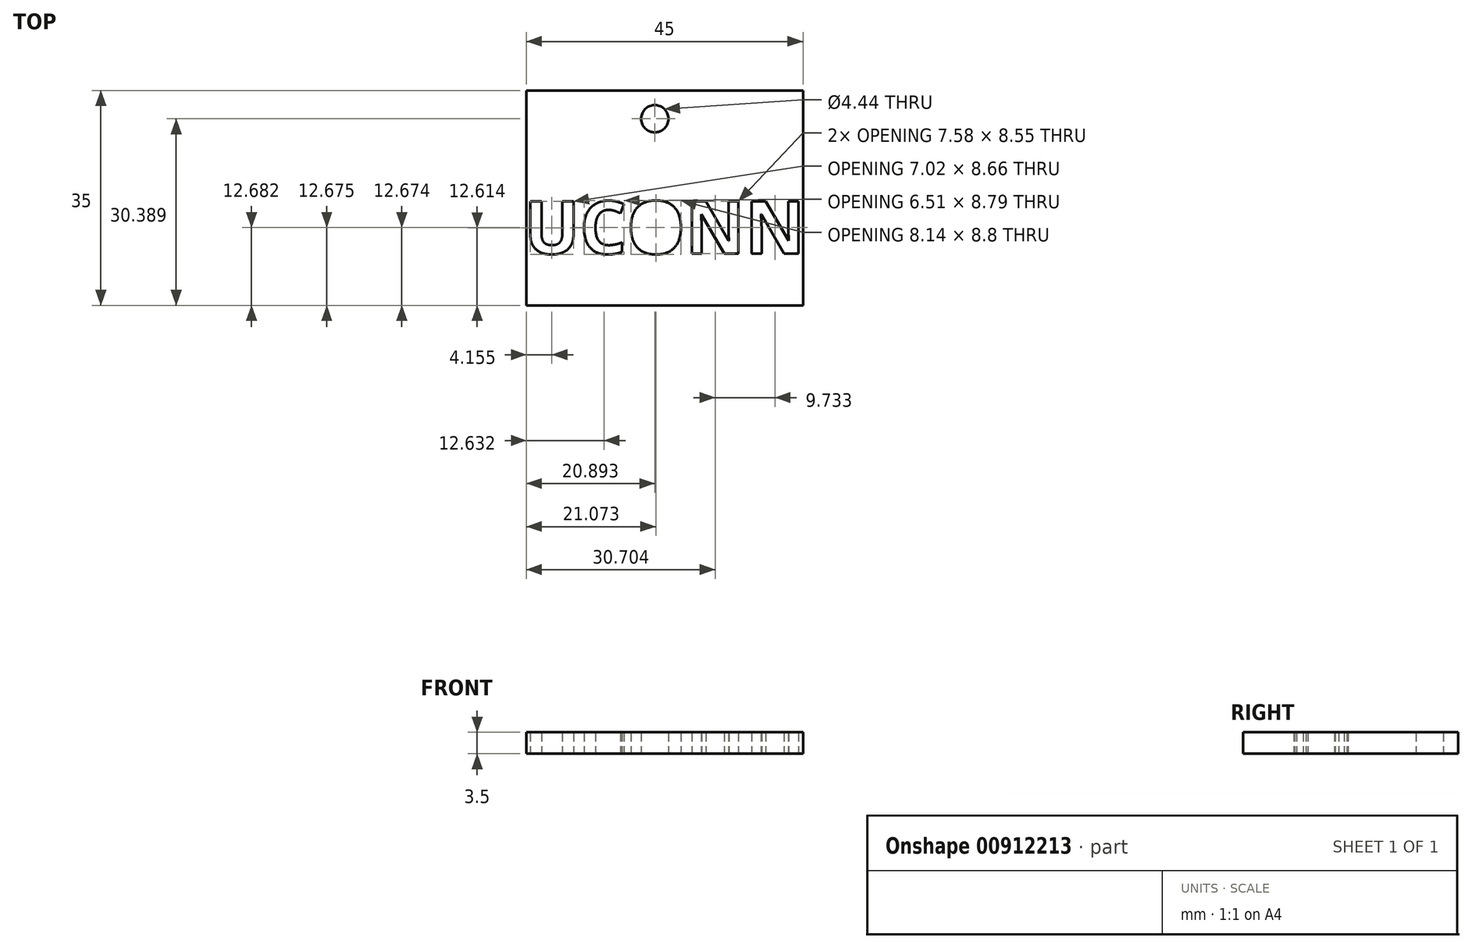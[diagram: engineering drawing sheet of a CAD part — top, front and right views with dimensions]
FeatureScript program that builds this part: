
annotation { "Feature Type Name" : "Feature", "Feature Type Description" : "" }
export const myFeature = defineFeature(function(context is Context, id is Id, definition is map)
    precondition{}
    {
        {
            var Q0;
            Q0=qCreatedBy(makeId("Top.planeOp"),FACE);
            var sketch = newSketch(context, id + "F0", { "sketchPlane" : qUnion([Q0])});
            skLineSegment(sketch, "E0.bottom", {"start": v(0, 0) * mm, "end": v(-45, 0) * mm});
            skLineSegment(sketch, "E0.top", {"start": v(0, 35) * mm, "end": v(-45, 35) * mm});
            skLineSegment(sketch, "E0.left", {"start": v(0, 0) * mm, "end": v(0, 35) * mm});
            skLineSegment(sketch, "E0.right", {"start": v(-45, 0) * mm, "end": v(-45, 35) * mm});
            skText(sketch, "E1", { "text": "UCONN", "fontName": "OpenSans-Bold.ttf"});
            skCircle(sketch, "E2", {"center": v(-24.1, 30.39) * mm, "radius": 2.22 * mm});
            const initialGuessF0  = {"E1": [-0.04537, 0.0084, 1, 0, 0.00862]};
            skSetInitialGuess(sketch, initialGuessF0);
            skSolve(sketch);
        }
        {
            var Q0;
            Q0=makeQuery(id+"F0.imprint","IMPRINT",FACE,{"disambiguationData":[TD([[makeQuery(id+"F0.imprint","IMPRINT",EDGE,{"derivedFrom":sQuery(id+"F0.wireOp",EDGE,"E0.bottom")}),-1.0]])]});
            extrude(context, id + "F1", {"entities" : qUnion([Q0]), "depth" : 3.5 * mm, "offsetDistance" : 25 * mm});
        }
    });
